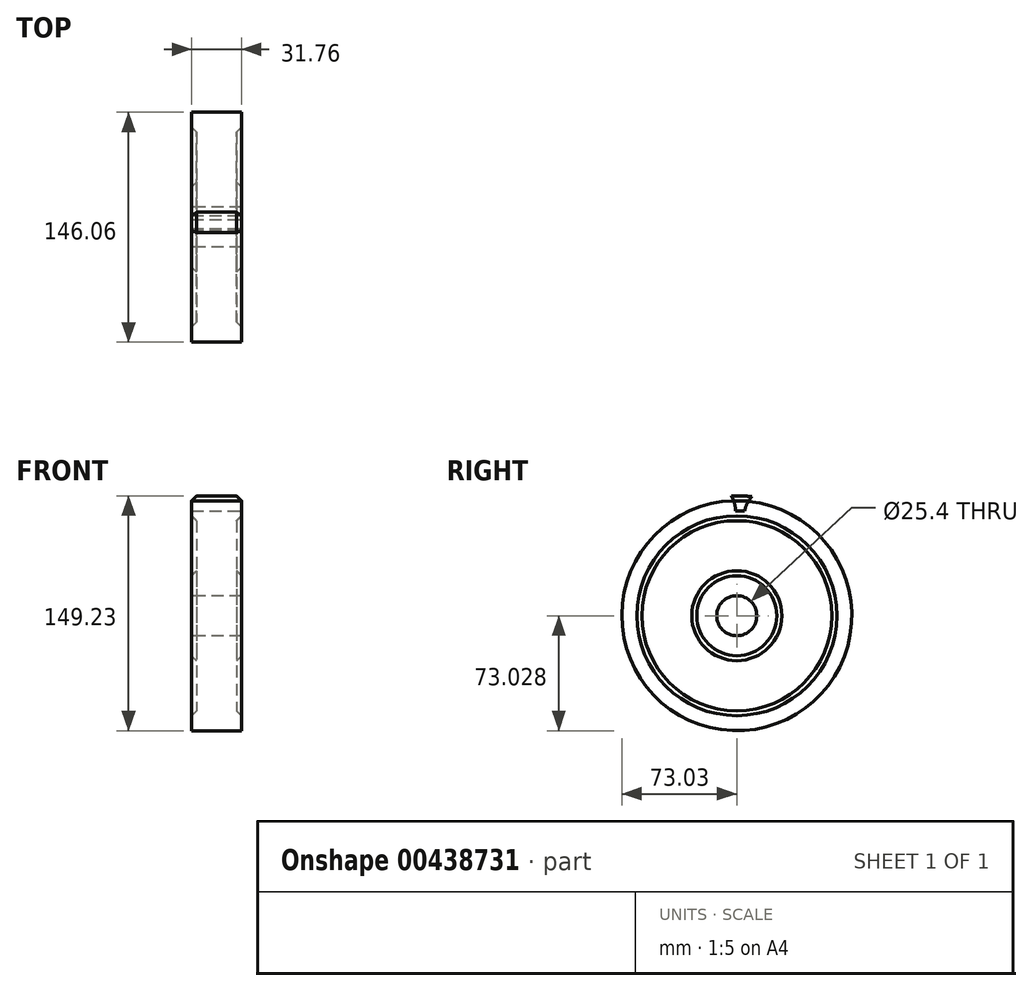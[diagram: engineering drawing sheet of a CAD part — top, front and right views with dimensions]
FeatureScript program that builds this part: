
annotation { "Feature Type Name" : "Feature", "Feature Type Description" : "" }
export const myFeature = defineFeature(function(context is Context, id is Id, definition is map)
    precondition{}
    {
        {
            var Q0;
            Q0=qCreatedBy(makeId("Front.planeOp"),FACE);
            var sketch = newSketch(context, id + "F0", { "sketchPlane" : qUnion([Q0])});
            skLineSegment(sketch, "E0", {"start": v(0, 41.77) * mm, "end": v(0, -21.73) * mm});
            skLineSegment(sketch, "E1", {"start": v(0, 41.77) * mm, "end": v(12.7, 41.77) * mm});
            skLineSegment(sketch, "E2", {"start": v(12.7, 41.77) * mm, "end": v(15.88, 38.6) * mm});
            skLineSegment(sketch, "E3", {"start": v(15.87, 38.6) * mm, "end": v(15.87, 29.07) * mm});
            skLineSegment(sketch, "E4", {"start": v(15.88, 29.07) * mm, "end": v(12.7, 25.9) * mm});
            skLineSegment(sketch, "E5", {"start": v(12.7, 25.9) * mm, "end": v(12.7, -5.86) * mm});
            skLineSegment(sketch, "E6", {"start": v(12.7, -5.86) * mm, "end": v(15.87, -9.03) * mm});
            skLineSegment(sketch, "E7", {"start": v(15.87, -9.03) * mm, "end": v(15.87, -21.73) * mm});
            skLineSegment(sketch, "E8", {"start": v(15.87, -21.73) * mm, "end": v(0, -21.73) * mm});
            skLineSegment(sketch, "E9", {"start": v(0, -21.73) * mm, "end": v(0, -34.43) * mm});
            skLineSegment(sketch, "E10", {"start": v(0, -34.43) * mm, "end": v(11.26, -34.43) * mm});
            skLineSegment(sketch, "E11.MirrorCS", {"start": v(0, 41.77) * mm, "end": v(-12.7, 41.77) * mm});
            skLineSegment(sketch, "E12.MirrorCS", {"start": v(-12.7, 41.77) * mm, "end": v(-15.88, 38.6) * mm});
            skLineSegment(sketch, "E13.MirrorCS", {"start": v(-15.88, 38.6) * mm, "end": v(-15.88, 29.07) * mm});
            skLineSegment(sketch, "E14.MirrorCS", {"start": v(-15.88, 29.07) * mm, "end": v(-12.7, 25.9) * mm});
            skLineSegment(sketch, "E15.MirrorCS", {"start": v(-12.7, 25.9) * mm, "end": v(-12.7, -5.86) * mm});
            skLineSegment(sketch, "E16.MirrorCS", {"start": v(-12.7, -5.86) * mm, "end": v(-15.87, -9.03) * mm});
            skLineSegment(sketch, "E17.MirrorCS", {"start": v(-15.88, -9.03) * mm, "end": v(-15.88, -21.73) * mm});
            skLineSegment(sketch, "E18.MirrorCS", {"start": v(-15.88, -21.73) * mm, "end": v(0, -21.73) * mm});
            skSolve(sketch);
        }
        {
            var Q0;
            Q0=makeQuery(id+"F0.imprint","IMPRINT",FACE,{"disambiguationData":[TD([[makeQuery(id+"F0.imprint","IMPRINT",EDGE,{"derivedFrom":sQuery(id+"F0.wireOp",EDGE,"E0")}),-1.0]])]});
            var Q1;
            Q1=makeQuery(id+"F0.imprint","IMPRINT",FACE,{"disambiguationData":[TD([[makeQuery(id+"F0.imprint","IMPRINT",EDGE,{"derivedFrom":sQuery(id+"F0.wireOp",EDGE,"E0")}),1.0]])]});
            var Q2;
            Q2=sQuery(id+"F0.wireOp",EDGE,"E10");
            revolve(context, id + "F1", {"entities" : qUnion([Q0, Q1]), "axis" : qUnion([Q2]), "revolveType" : RevolveType.FULL});
        }
        {
            var Q0;
            Q0=makeQuery(id+"F1.opRevolve","SWEPT_FACE",FACE,{"disambiguationData":[OSD([sQuery(id+"F0.wireOp",EDGE,"E3")])]});
            var sketch = newSketch(context, id + "F2", { "sketchPlane" : qUnion([Q0])});
            skLineSegment(sketch, "E19", {"start": v(0, -34.43) * mm, "end": v(0, 79.77) * mm});
            skLineSegment(sketch, "E20", {"start": v(-0.74, 32.24) * mm, "end": v(4.98, 32.24) * mm});
            skArc(sketch, "E21", {"start": v(9.57, 41.16) * mm, "mid": v(6.68, 37.01) * mm, "end": v(4.98, 32.24) * mm});
            skArc(sketch, "E22", {"start": v(-0.74, 32.24) * mm, "mid": v(-1.5, 37.15) * mm, "end": v(-3.51, 41.69) * mm});
            skArc(sketch, "E23", {"start": v(9.57, 41.16) * mm, "mid": v(3.04, 41.7) * mm, "end": v(-3.51, 41.69) * mm});
            skCircle(sketch, "E24.0", {"center": v(0, -34.43) * mm, "radius": 76.2 * mm});
            skSolve(sketch);
        }
        {
            var Q0;
            {var subQ0=sQuery(id+"F2.wireOp",EDGE,"E20");var subQ5=sQuery(id+"F2.wireOp",EDGE,"E22");var subQ6=makeQuery(id+"F2.imprint","INTERSECT",VERTEX,{"derivedFrom":[subQ0,subQ5]});Q0=makeQuery(id+"F2.imprint","IMPRINT",FACE,{"disambiguationData":[TD([[makeQuery(id+"F2.imprint","IMPRINT",EDGE,{"disambiguationData":[TD([[subQ6,-1.0]])],"derivedFrom":subQ0}),1.0]])]});}
            var Q1;
            {var subQ0=sQuery(id+"F2.wireOp",EDGE,"E20");var subQ5=sQuery(id+"F2.wireOp",EDGE,"E21");var subQ6=makeQuery(id+"F2.imprint","INTERSECT",VERTEX,{"derivedFrom":[subQ0,subQ5]});Q1=makeQuery(id+"F2.imprint","IMPRINT",FACE,{"disambiguationData":[TD([[makeQuery(id+"F2.imprint","IMPRINT",EDGE,{"disambiguationData":[TD([[subQ6,1.0]])],"derivedFrom":subQ0}),1.0]])]});}
            var Q2;
            {var subQ0=sQuery(id+"F2.wireOp",EDGE,"E24.0");var subQ5=sQuery(id+"F2.wireOp",EDGE,"E22");var subQ6=makeQuery(id+"F2.imprint","INTERSECT",VERTEX,{"derivedFrom":[subQ5,subQ0]});Q2=makeQuery(id+"F2.imprint","IMPRINT",FACE,{"disambiguationData":[TD([[makeQuery(id+"F2.imprint","IMPRINT",EDGE,{"disambiguationData":[TD([[subQ6,1.0]])],"derivedFrom":subQ0}),1.0]])]});}
            var Q3;
            {var subQ0=sQuery(id+"F2.wireOp",EDGE,"E24.0");var subQ5=sQuery(id+"F2.wireOp",EDGE,"E21");var subQ6=makeQuery(id+"F2.imprint","INTERSECT",VERTEX,{"derivedFrom":[subQ5,subQ0]});Q3=makeQuery(id+"F2.imprint","IMPRINT",FACE,{"disambiguationData":[TD([[makeQuery(id+"F2.imprint","IMPRINT",EDGE,{"disambiguationData":[TD([[subQ6,-1.0]])],"derivedFrom":subQ0}),1.0]])]});}
            extrude(context, id + "F3", {"entities" : qUnion([Q0, Q1, Q2, Q3]), "operationType" : NewBodyOperationType.REMOVE, "oppositeDirection" : true, "depth" : 50.8 * mm});
        }
    });
